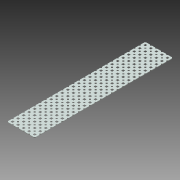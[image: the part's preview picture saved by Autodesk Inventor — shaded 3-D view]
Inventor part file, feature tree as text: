
AUTODESK INVENTOR PART (.ipt)
format: ipt  version: 2013 (Build 170138000, 138)  size: 2,302,464 bytes
history: native  units: mm (DEFAULTED — no unit token found)
features: other x125, extrude x125, imported_body x1, pattern_linear x1, sketch x1
ambient origin geometry x8: Origin, YZ Plane, XZ Plane, XY Plane, X Axis, Y Axis, Z Axis, Center Point
bodies: Solid1 (feature_tree)
feature tree (253):
  imported_body  "Base1"
  pattern_linear  "Rectangular Pattern1"  Spacing1=0.0mm  [1 undecoded]
  sketch  "Sketch1"  dims[d1=1.1684mm d2=0.0mm d3=250.0mm d5=12.7mm d6=50.0mm d8=12.7mm d9=0.0mm d10=0.0mm d11=0.0mm d12=0.0mm d13=0.0mm d14=0.0mm d15=0.0mm d16=0.0mm d17=0.0mm d18=0.0mm d19=0.0mm d20=0.0mm d21=0.0mm d22=0.0mm d23=0.0mm d24=0.0mm d25=0.0mm d26=0.0mm d27=0.0mm d28=0.0mm d29=0.0mm d30=0.0mm d31=0.0mm d32=0.0mm d33=0.0mm d34=0.0mm d35=0.0mm d36=0.0mm d37=0.0mm d38=0.0mm d39=0.0mm d40=0.0mm d41=0.0mm d42=0.0mm d43=0.0mm d44=0.0mm d45=0.0mm d46=0.0mm d47=0.0mm d48=0.0mm d49=0.0mm d50=0.0mm d51=0.0mm d52=0.0mm d53=0.0mm d54=0.0mm d55=0.0mm d56=0.0mm d57=0.0mm d58=0.0mm d59=0.0mm d60=0.0mm d61=0.0mm d62=0.0mm d63=0.0mm d64=0.0mm d65=0.0mm d66=0.0mm d67=0.0mm d68=0.0mm d69=0.0mm d70=0.0mm d71=0.0mm d72=0.0mm d73=0.0mm d74=0.0mm d75=0.0mm d76=0.0mm d77=0.0mm d78=0.0mm d79=0.0mm d80=0.0mm d81=0.0mm d82=0.0mm d83=0.0mm d84=0.0mm d85=0.0mm d86=0.0mm d87=0.0mm d88=0.0mm d89=0.0mm d90=0.0mm d91=0.0mm d92=0.0mm d93=0.0mm d94=0.0mm d95=0.0mm d96=0.0mm d97=0.0mm d98=0.0mm d99=0.0mm d100=0.0mm d101=0.0mm d102=0.0mm d103=0.0mm d104=0.0mm d105=0.0mm d106=0.0mm d107=0.0mm d108=0.0mm d109=0.0mm d110=0.0mm d111=0.0mm d112=0.0mm d113=0.0mm d114=0.0mm d115=0.0mm d116=0.0mm d117=0.0mm d118=0.0mm d119=0.0mm d120=0.0mm d121=0.0mm d122=0.0mm d123=0.0mm d124=0.0mm d125=0.0mm d126=0.0mm d127=0.0mm d128=0.0mm d129=0.0mm d130=0.0mm d131=0.0mm d132=0.0mm d133=0.0mm d134=0.0mm d135=0.0mm d136=0.0mm d137=0.0mm d138=0.0mm d139=0.0mm d140=0.0mm d141=0.0mm d142=0.0mm d143=0.0mm d144=0.0mm d145=0.0mm d146=0.0mm d147=0.0mm d148=0.0mm d149=0.0mm d150=0.0mm d151=0.0mm d152=0.0mm d153=0.0mm d154=0.0mm d155=0.0mm d156=0.0mm d157=0.0mm d158=0.0mm d159=0.0mm d160=0.0mm d161=0.0mm d162=0.0mm d163=0.0mm d164=0.0mm d165=0.0mm d166=0.0mm d167=0.0mm d168=0.0mm d169=0.0mm d170=0.0mm d171=0.0mm d172=0.0mm d173=0.0mm d174=0.0mm d175=0.0mm d176=0.0mm d177=0.0mm d178=0.0mm d179=0.0mm d180=0.0mm d181=0.0mm d182=0.0mm d183=0.0mm d184=0.0mm d185=0.0mm d186=0.0mm d187=0.0mm d188=0.0mm d189=0.0mm d190=0.0mm d191=0.0mm d192=0.0mm d193=0.0mm d194=0.0mm d195=0.0mm d196=0.0mm d197=0.0mm d198=0.0mm d199=0.0mm d200=0.0mm d201=0.0mm d202=0.0mm d203=0.0mm d204=0.0mm d205=0.0mm d206=0.0mm d207=0.0mm d208=0.0mm d209=0.0mm d210=0.0mm d211=0.0mm d212=0.0mm d213=0.0mm d214=0.0mm d215=0.0mm d216=0.0mm d217=0.0mm d218=0.0mm d219=0.0mm d220=0.0mm d221=0.0mm d222=0.0mm d223=0.0mm d224=0.0mm d225=0.0mm d226=0.0mm d227=0.0mm d228=0.0mm d229=0.0mm d230=0.0mm d231=0.0mm d232=0.0mm d233=0.0mm d234=0.0mm d235=0.0mm d236=0.0mm d237=0.0mm d238=0.0mm d239=0.0mm d240=0.0mm d241=0.0mm d242=0.0mm d243=0.0mm d244=0.0mm d245=0.0mm d246=0.0mm d247=0.0mm d248=0.0mm d249=0.0mm d250=0.0mm d251=0.0mm d252=0.0mm d253=0.0mm d254=0.0mm d255=0.0mm d256=0.0mm d257=0.0mm d258=0.0mm]
  other  "Srf1"
  other  "Srf2"
  other  "Srf3"
  other  "Srf4"
  other  "Srf5"
  other  "Srf6"
  other  "Srf7"
  other  "Srf8"
  other  "Srf9"
  other  "Srf10"
  other  "Srf11"
  other  "Srf12"
  other  "Srf13"
  other  "Srf14"
  other  "Srf15"
  other  "Srf16"
  other  "Srf17"
  other  "Srf18"
  other  "Srf19"
  other  "Srf20"
  other  "Srf21"
  other  "Srf22"
  other  "Srf23"
  other  "Srf24"
  other  "Srf25"
  other  "Srf26"
  other  "Srf27"
  other  "Srf28"
  other  "Srf29"
  other  "Srf30"
  other  "Srf31"
  other  "Srf32"
  other  "Srf33"
  other  "Srf34"
  other  "Srf35"
  other  "Srf36"
  other  "Srf37"
  other  "Srf38"
  other  "Srf39"
  other  "Srf40"
  other  "Srf41"
  other  "Srf42"
  other  "Srf43"
  other  "Srf44"
  other  "Srf45"
  other  "Srf46"
  other  "Srf47"
  other  "Srf48"
  other  "Srf49"
  other  "Srf50"
  other  "Srf51"
  other  "Srf52"
  other  "Srf53"
  other  "Srf54"
  other  "Srf55"
  other  "Srf56"
  other  "Srf57"
  other  "Srf58"
  other  "Srf59"
  other  "Srf60"
  other  "Srf61"
  other  "Srf62"
  other  "Srf63"
  other  "Srf64"
  other  "Srf65"
  other  "Srf66"
  other  "Srf67"
  other  "Srf68"
  other  "Srf69"
  other  "Srf70"
  other  "Srf71"
  other  "Srf72"
  other  "Srf73"
  other  "Srf74"
  other  "Srf75"
  other  "Srf76"
  other  "Srf77"
  other  "Srf78"
  other  "Srf79"
  other  "Srf80"
  other  "Srf81"
  other  "Srf82"
  other  "Srf83"
  other  "Srf84"
  other  "Srf85"
  other  "Srf86"
  other  "Srf87"
  other  "Srf88"
  other  "Srf89"
  other  "Srf90"
  other  "Srf91"
  other  "Srf92"
  other  "Srf93"
  other  "Srf94"
  other  "Srf95"
  other  "Srf96"
  other  "Srf97"
  other  "Srf98"
  other  "Srf99"
  other  "Srf100"
  other  "Srf101"
  other  "Srf102"
  other  "Srf103"
  other  "Srf104"
  other  "Srf105"
  other  "Srf106"
  other  "Srf107"
  other  "Srf108"
  other  "Srf109"
  other  "Srf110"
  other  "Srf111"
  other  "Srf112"
  other  "Srf113"
  other  "Srf114"
  other  "Srf115"
  other  "Srf116"
  other  "Srf117"
  other  "Srf118"
  other  "Srf119"
  other  "Srf120"
  other  "Srf121"
  other  "Srf122"
  other  "Srf123"
  other  "Srf124"
  other  "Srf125"
  extrude  "ExtrusionSrf1"  Depth=250.0mm
  extrude  "ExtrusionSrf2"  Depth=12.7mm
  extrude  "ExtrusionSrf3"  Depth=50.0mm
  extrude  "ExtrusionSrf4"  TaperAngle=0.0deg  [1 undecoded]
  extrude  "ExtrusionSrf5"  TaperAngle=0.0deg  [1 undecoded]
  extrude  "ExtrusionSrf6"  TaperAngle=0.0deg  [1 undecoded]
  extrude  "ExtrusionSrf7"  TaperAngle=0.0deg  [1 undecoded]
  extrude  "ExtrusionSrf8"  TaperAngle=0.0deg  [1 undecoded]
  extrude  "ExtrusionSrf9"  TaperAngle=0.0deg  [1 undecoded]
  extrude  "ExtrusionSrf10"  TaperAngle=0.0deg  [1 undecoded]
  extrude  "ExtrusionSrf11"  TaperAngle=0.0deg  [1 undecoded]
  extrude  "ExtrusionSrf12"  TaperAngle=0.0deg  [1 undecoded]
  extrude  "ExtrusionSrf13"  TaperAngle=0.0deg  [1 undecoded]
  extrude  "ExtrusionSrf14"  TaperAngle=0.0deg  [1 undecoded]
  extrude  "ExtrusionSrf15"  TaperAngle=0.0deg  [1 undecoded]
  extrude  "ExtrusionSrf16"  TaperAngle=0.0deg  [1 undecoded]
  extrude  "ExtrusionSrf17"  TaperAngle=0.0deg  [1 undecoded]
  extrude  "ExtrusionSrf18"  TaperAngle=0.0deg  [1 undecoded]
  extrude  "ExtrusionSrf19"  TaperAngle=0.0deg  [1 undecoded]
  extrude  "ExtrusionSrf20"  TaperAngle=0.0deg  [1 undecoded]
  extrude  "ExtrusionSrf21"  TaperAngle=0.0deg  [1 undecoded]
  extrude  "ExtrusionSrf22"  TaperAngle=0.0deg  [1 undecoded]
  extrude  "ExtrusionSrf23"  TaperAngle=0.0deg  [1 undecoded]
  extrude  "ExtrusionSrf24"  TaperAngle=0.0deg  [1 undecoded]
  extrude  "ExtrusionSrf25"  TaperAngle=0.0deg  [1 undecoded]
  extrude  "ExtrusionSrf26"  TaperAngle=0.0deg  [1 undecoded]
  extrude  "ExtrusionSrf27"  TaperAngle=0.0deg  [1 undecoded]
  extrude  "ExtrusionSrf28"  TaperAngle=0.0deg  [1 undecoded]
  extrude  "ExtrusionSrf29"  TaperAngle=0.0deg  [1 undecoded]
  extrude  "ExtrusionSrf30"  TaperAngle=0.0deg  [1 undecoded]
  extrude  "ExtrusionSrf31"  TaperAngle=0.0deg  [1 undecoded]
  extrude  "ExtrusionSrf32"  TaperAngle=0.0deg  [1 undecoded]
  extrude  "ExtrusionSrf33"  TaperAngle=0.0deg  [1 undecoded]
  extrude  "ExtrusionSrf34"  TaperAngle=0.0deg  [1 undecoded]
  extrude  "ExtrusionSrf35"  TaperAngle=0.0deg  [1 undecoded]
  extrude  "ExtrusionSrf36"  TaperAngle=0.0deg  [1 undecoded]
  extrude  "ExtrusionSrf37"  TaperAngle=0.0deg  [1 undecoded]
  extrude  "ExtrusionSrf38"  TaperAngle=0.0deg  [1 undecoded]
  extrude  "ExtrusionSrf39"  TaperAngle=0.0deg  [1 undecoded]
  extrude  "ExtrusionSrf40"  TaperAngle=0.0deg  [1 undecoded]
  extrude  "ExtrusionSrf41"  TaperAngle=0.0deg  [1 undecoded]
  extrude  "ExtrusionSrf42"  TaperAngle=0.0deg  [1 undecoded]
  extrude  "ExtrusionSrf43"  TaperAngle=0.0deg  [1 undecoded]
  extrude  "ExtrusionSrf44"  TaperAngle=0.0deg  [1 undecoded]
  extrude  "ExtrusionSrf45"  TaperAngle=0.0deg  [1 undecoded]
  extrude  "ExtrusionSrf46"  TaperAngle=0.0deg  [1 undecoded]
  extrude  "ExtrusionSrf47"  TaperAngle=0.0deg  [1 undecoded]
  extrude  "ExtrusionSrf48"  TaperAngle=0.0deg  [1 undecoded]
  extrude  "ExtrusionSrf49"  TaperAngle=0.0deg  [1 undecoded]
  extrude  "ExtrusionSrf50"  TaperAngle=0.0deg  [1 undecoded]
  extrude  "ExtrusionSrf51"  TaperAngle=0.0deg  [1 undecoded]
  extrude  "ExtrusionSrf52"  TaperAngle=0.0deg  [1 undecoded]
  extrude  "ExtrusionSrf53"  TaperAngle=0.0deg  [1 undecoded]
  extrude  "ExtrusionSrf54"  TaperAngle=0.0deg  [1 undecoded]
  extrude  "ExtrusionSrf55"  TaperAngle=0.0deg  [1 undecoded]
  extrude  "ExtrusionSrf56"  TaperAngle=0.0deg  [1 undecoded]
  extrude  "ExtrusionSrf57"  TaperAngle=0.0deg  [1 undecoded]
  extrude  "ExtrusionSrf58"  TaperAngle=0.0deg  [1 undecoded]
  extrude  "ExtrusionSrf59"  TaperAngle=0.0deg  [1 undecoded]
  extrude  "ExtrusionSrf60"  TaperAngle=0.0deg  [1 undecoded]
  extrude  "ExtrusionSrf61"  TaperAngle=0.0deg  [1 undecoded]
  extrude  "ExtrusionSrf62"  TaperAngle=0.0deg  [1 undecoded]
  extrude  "ExtrusionSrf63"  TaperAngle=0.0deg  [1 undecoded]
  extrude  "ExtrusionSrf64"  TaperAngle=0.0deg  [1 undecoded]
  extrude  "ExtrusionSrf65"  TaperAngle=0.0deg  [1 undecoded]
  extrude  "ExtrusionSrf66"  TaperAngle=0.0deg  [1 undecoded]
  extrude  "ExtrusionSrf67"  TaperAngle=0.0deg  [1 undecoded]
  extrude  "ExtrusionSrf68"  TaperAngle=0.0deg  [1 undecoded]
  extrude  "ExtrusionSrf69"  TaperAngle=0.0deg  [1 undecoded]
  extrude  "ExtrusionSrf70"  TaperAngle=0.0deg  [1 undecoded]
  extrude  "ExtrusionSrf71"  TaperAngle=0.0deg  [1 undecoded]
  extrude  "ExtrusionSrf72"  TaperAngle=0.0deg  [1 undecoded]
  extrude  "ExtrusionSrf73"  TaperAngle=0.0deg  [1 undecoded]
  extrude  "ExtrusionSrf74"  TaperAngle=0.0deg  [1 undecoded]
  extrude  "ExtrusionSrf75"  TaperAngle=0.0deg  [1 undecoded]
  extrude  "ExtrusionSrf76"  TaperAngle=0.0deg  [1 undecoded]
  extrude  "ExtrusionSrf77"  TaperAngle=0.0deg  [1 undecoded]
  extrude  "ExtrusionSrf78"  TaperAngle=0.0deg  [1 undecoded]
  extrude  "ExtrusionSrf79"  TaperAngle=0.0deg  [1 undecoded]
  extrude  "ExtrusionSrf80"  TaperAngle=0.0deg  [1 undecoded]
  extrude  "ExtrusionSrf81"  TaperAngle=0.0deg  [1 undecoded]
  extrude  "ExtrusionSrf82"  TaperAngle=0.0deg  [1 undecoded]
  extrude  "ExtrusionSrf83"  TaperAngle=0.0deg  [1 undecoded]
  extrude  "ExtrusionSrf84"  TaperAngle=0.0deg  [1 undecoded]
  extrude  "ExtrusionSrf85"  TaperAngle=0.0deg  [1 undecoded]
  extrude  "ExtrusionSrf86"  TaperAngle=0.0deg  [1 undecoded]
  extrude  "ExtrusionSrf87"  TaperAngle=0.0deg  [1 undecoded]
  extrude  "ExtrusionSrf88"  TaperAngle=0.0deg  [1 undecoded]
  extrude  "ExtrusionSrf89"  TaperAngle=0.0deg  [1 undecoded]
  extrude  "ExtrusionSrf90"  TaperAngle=0.0deg  [1 undecoded]
  extrude  "ExtrusionSrf91"  TaperAngle=0.0deg  [1 undecoded]
  extrude  "ExtrusionSrf92"  TaperAngle=0.0deg  [1 undecoded]
  extrude  "ExtrusionSrf93"  TaperAngle=0.0deg  [1 undecoded]
  extrude  "ExtrusionSrf94"  TaperAngle=0.0deg  [1 undecoded]
  extrude  "ExtrusionSrf95"  TaperAngle=0.0deg  [1 undecoded]
  extrude  "ExtrusionSrf96"  TaperAngle=0.0deg  [1 undecoded]
  extrude  "ExtrusionSrf97"  TaperAngle=0.0deg  [1 undecoded]
  extrude  "ExtrusionSrf98"  TaperAngle=0.0deg  [1 undecoded]
  extrude  "ExtrusionSrf99"  TaperAngle=0.0deg  [1 undecoded]
  extrude  "ExtrusionSrf100"  TaperAngle=0.0deg  [1 undecoded]
  extrude  "ExtrusionSrf101"  TaperAngle=0.0deg  [1 undecoded]
  extrude  "ExtrusionSrf102"  TaperAngle=0.0deg  [1 undecoded]
  extrude  "ExtrusionSrf103"  TaperAngle=0.0deg  [1 undecoded]
  extrude  "ExtrusionSrf104"  TaperAngle=0.0deg  [1 undecoded]
  extrude  "ExtrusionSrf105"  TaperAngle=0.0deg  [1 undecoded]
  extrude  "ExtrusionSrf106"  TaperAngle=0.0deg  [1 undecoded]
  extrude  "ExtrusionSrf107"  TaperAngle=0.0deg  [1 undecoded]
  extrude  "ExtrusionSrf108"  TaperAngle=0.0deg  [1 undecoded]
  extrude  "ExtrusionSrf109"  TaperAngle=0.0deg  [1 undecoded]
  extrude  "ExtrusionSrf110"  TaperAngle=0.0deg  [1 undecoded]
  extrude  "ExtrusionSrf111"  TaperAngle=0.0deg  [1 undecoded]
  extrude  "ExtrusionSrf112"  TaperAngle=0.0deg  [1 undecoded]
  extrude  "ExtrusionSrf113"  TaperAngle=0.0deg  [1 undecoded]
  extrude  "ExtrusionSrf114"  TaperAngle=0.0deg  [1 undecoded]
  extrude  "ExtrusionSrf115"  TaperAngle=0.0deg  [1 undecoded]
  extrude  "ExtrusionSrf116"  TaperAngle=0.0deg  [1 undecoded]
  extrude  "ExtrusionSrf117"  TaperAngle=0.0deg  [1 undecoded]
  extrude  "ExtrusionSrf118"  TaperAngle=0.0deg  [1 undecoded]
  extrude  "ExtrusionSrf119"  TaperAngle=0.0deg  [1 undecoded]
  extrude  "ExtrusionSrf120"  TaperAngle=0.0deg  [1 undecoded]
  extrude  "ExtrusionSrf121"  TaperAngle=0.0deg  [1 undecoded]
  extrude  "ExtrusionSrf122"  TaperAngle=0.0deg  [1 undecoded]
  extrude  "ExtrusionSrf123"  TaperAngle=0.0deg  [1 undecoded]
  extrude  "ExtrusionSrf124"  TaperAngle=0.0deg  [1 undecoded]
  extrude  "ExtrusionSrf125"  TaperAngle=0.0deg  [1 undecoded]
note: 123 required parameter values undecoded (feature->parameter linkage not recoverable at this tier; creation-order binding heuristic only, values carry confidence <= 0.55)
